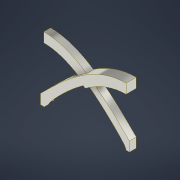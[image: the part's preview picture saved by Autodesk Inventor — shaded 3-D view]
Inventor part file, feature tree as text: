
AUTODESK INVENTOR PART (.ipt)
format: ipt  version: 2022 (Build 260153000, 153)  size: 405,504 bytes
history: native  units: in
note: dims shown in document units (in); Inventor stores cm internally (conversion verified against a paired STEP export)
features: sketch x4, other x4, extrude x3, plane x2, projected_geometry x2, revolve x1
ambient origin geometry x8: Origin, YZ Plane, XZ Plane, XY Plane, X Axis, Y Axis, Z Axis, Center Point
bodies: Body1 (feature_tree)
feature tree (16):
  sketch  "Sketch1"  dims[d4=0.0in d5=90.0deg d6=0.0in d7=90.0deg]
  extrude  "Extrusion3"  TaperAngle=0.0deg  [1 undecoded]
  extrude  "Extrusion4"  Depth=0.125in
  plane  "Work Plane1"
  revolve  "Revolution1"  [1 undecoded]
  extrude  "Extrusion5"  Depth=0.125in TaperAngle=0.0deg
  plane  "Work Plane2"
  sketch  "Sketch4"  dims[d16=0.1875in d17=0.0in d18=0.125in d19=0.0in d28=0.0in d29=180.0deg d30=0.0in d31=180.0deg d32=90.0deg d33=5.0in d34=0.0in]
  other  "2D Equation Curve1"
  other  "2D Equation Curve2"
  sketch  "Sketch2"  dims[d8=0.125in d9=0.125in]
  other  "2D Equation Curve3"
  other  "2D Equation Curve4"
  sketch  "Sketch3"  dims[d14=0.05in d15=0.05in]
  projected_geometry  "Projected Loop1"
  projected_geometry  "Projected Loop2"
note: 2 required parameter values undecoded (feature->parameter linkage not recoverable at this tier; creation-order binding heuristic only, values carry confidence <= 0.55)